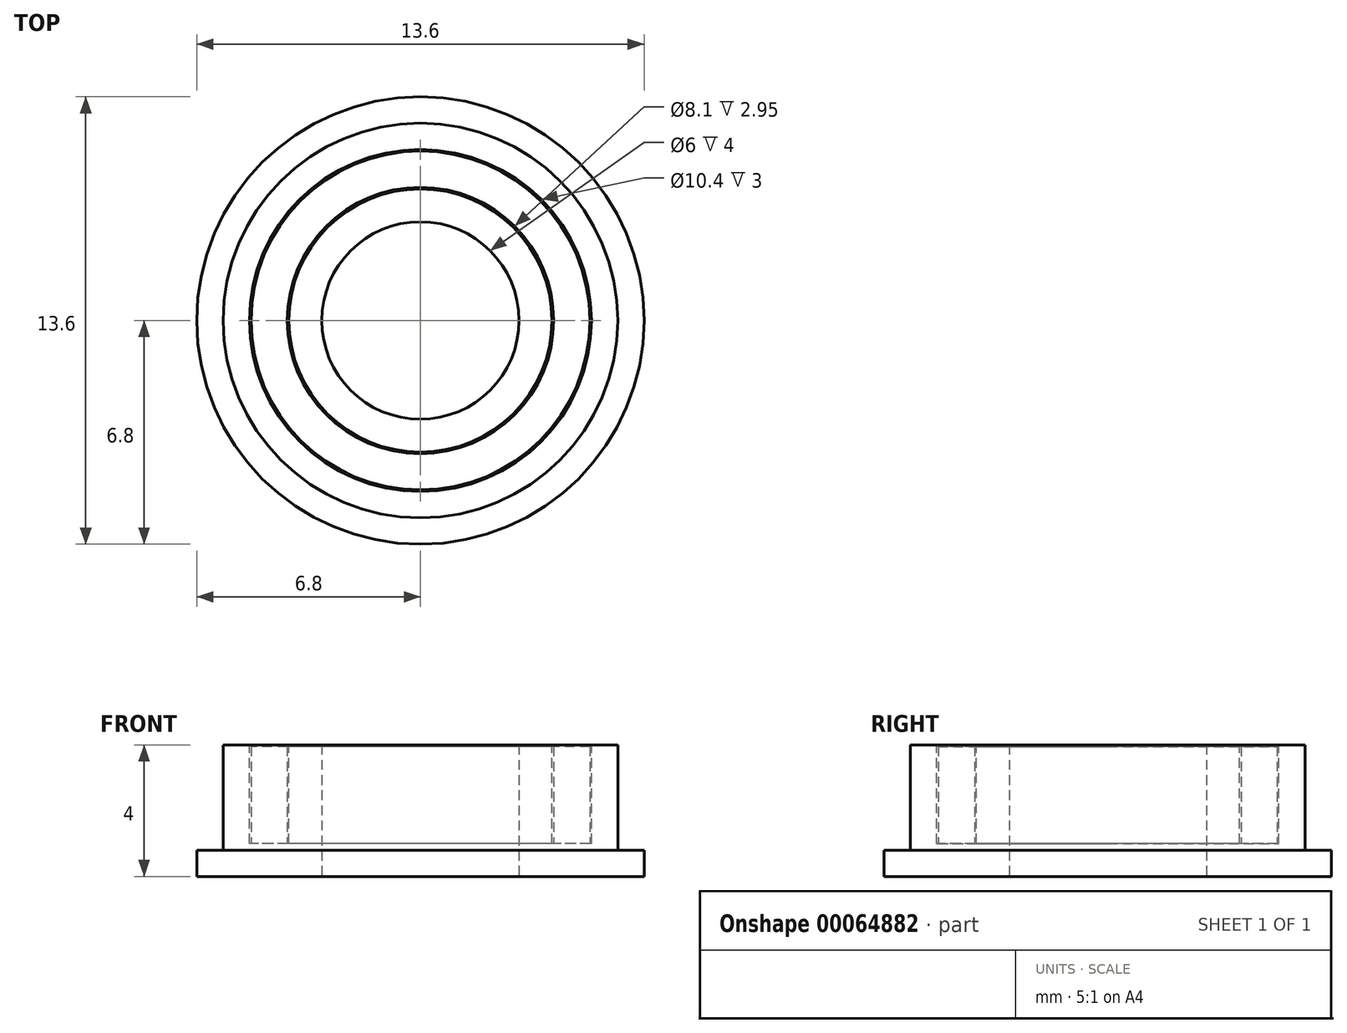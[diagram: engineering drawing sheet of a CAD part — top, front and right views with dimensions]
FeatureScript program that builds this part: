
annotation { "Feature Type Name" : "Feature", "Feature Type Description" : "" }
export const myFeature = defineFeature(function(context is Context, id is Id, definition is map)
    precondition{}
    {
        {
            var Q0;
            Q0=qCreatedBy(makeId("Front.planeOp"),FACE);
            var sketch = newSketch(context, id + "F0", { "sketchPlane" : qUnion([Q0])});
            skLineSegment(sketch, "E0.bottom", {"start": v(0, 0) * mm, "end": v(6, 0) * mm, "construction": true});
            skLineSegment(sketch, "E0.top", {"start": v(0, 4) * mm, "end": v(6, 4) * mm, "construction": true});
            skLineSegment(sketch, "E0.left", {"start": v(0, 0) * mm, "end": v(0, 4) * mm, "construction": true});
            skLineSegment(sketch, "E0.right", {"start": v(6, 0) * mm, "end": v(6, 4) * mm, "construction": true});
            skLineSegment(sketch, "E1", {"start": v(0, 0) * mm, "end": v(3, 0) * mm});
            skLineSegment(sketch, "E2", {"start": v(3, 0) * mm, "end": v(6.8, 0) * mm});
            skLineSegment(sketch, "E3", {"start": v(6.8, 0) * mm, "end": v(6.8, 0.8) * mm});
            skLineSegment(sketch, "E4", {"start": v(6.8, 0.8) * mm, "end": v(6, 0.8) * mm});
            skLineSegment(sketch, "E5", {"start": v(6, 0.8) * mm, "end": v(6, 4) * mm});
            skLineSegment(sketch, "E6", {"start": v(6, 4) * mm, "end": v(3, 4) * mm});
            skLineSegment(sketch, "E7", {"start": v(3, 4) * mm, "end": v(3, 0) * mm});
            skSolve(sketch);
        }
        {
            var Q0;
            Q0=makeQuery(id+"F0.imprint","IMPRINT",FACE,{"disambiguationData":[TD([[makeQuery(id+"F0.imprint","IMPRINT",EDGE,{"derivedFrom":sQuery(id+"F0.wireOp",EDGE,"E2")}),1.0]])]});
            var Q1;
            Q1=sQuery(id+"F0.wireOp",EDGE,"E0.left");
            revolve(context, id + "F1", {"entities" : qUnion([Q0]), "axis" : qUnion([Q1]), "revolveType" : RevolveType.FULL});
        }
        {
            var Q0;
            Q0=makeQuery(id+"F1.opRevolve","SWEPT_FACE",FACE,{"disambiguationData":[OSD([sQuery(id+"F0.wireOp",EDGE,"E6")])]});
            var sketch = newSketch(context, id + "F2", { "sketchPlane" : qUnion([Q0])});
            skCircle(sketch, "E8.0", {"center": v(0, 0) * mm, "radius": 5.2 * mm});
            skCircle(sketch, "E9.0", {"center": v(0, 0) * mm, "radius": 4 * mm});
            skSolve(sketch);
        }
        {
            var Q0;
            Q0=makeQuery(id+"F2.imprint","IMPRINT",FACE,{"disambiguationData":[TD([[makeQuery(id+"F2.imprint","IMPRINT",EDGE,{"derivedFrom":sQuery(id+"F2.wireOp",EDGE,"E8.0")}),1.0]])]});
            extrude(context, id + "F3", {"entities" : qUnion([Q0]), "operationType" : NewBodyOperationType.REMOVE, "oppositeDirection" : true, "depth" : 3 * mm});
        }
        {
            var Q0;
            Q0=makeQuery(id+"F3.boolean.opBoolean","COPY",FACE,{"derivedFrom":makeQuery(id+"F3.opExtrude","CAP_FACE",FACE,{"disambiguationData":[OSD([sQuery(id+"F2.wireOp",EDGE,"E8.0"),sQuery(id+"F2.wireOp",EDGE,"E9.0")])],"isStart":false})});
            var sketch = newSketch(context, id + "F4", { "sketchPlane" : qUnion([Q0])});
            skCircle(sketch, "E10.0", {"center": v(0, 0) * mm, "radius": 4.05 * mm});
            skCircle(sketch, "E11.0", {"center": v(0, 0) * mm, "radius": 5.15 * mm});
            skSolve(sketch);
        }
        {
            var Q0;
            Q0=makeQuery(id+"F4.imprint","IMPRINT",FACE,{"disambiguationData":[TD([[makeQuery(id+"F4.imprint","IMPRINT",EDGE,{"derivedFrom":sQuery(id+"F4.wireOp",EDGE,"E10.0")}),-1.0]])]});
            extrude(context, id + "F5", {"entities" : qUnion([Q0]), "depth" : 2.95 * mm});
        }
    });
